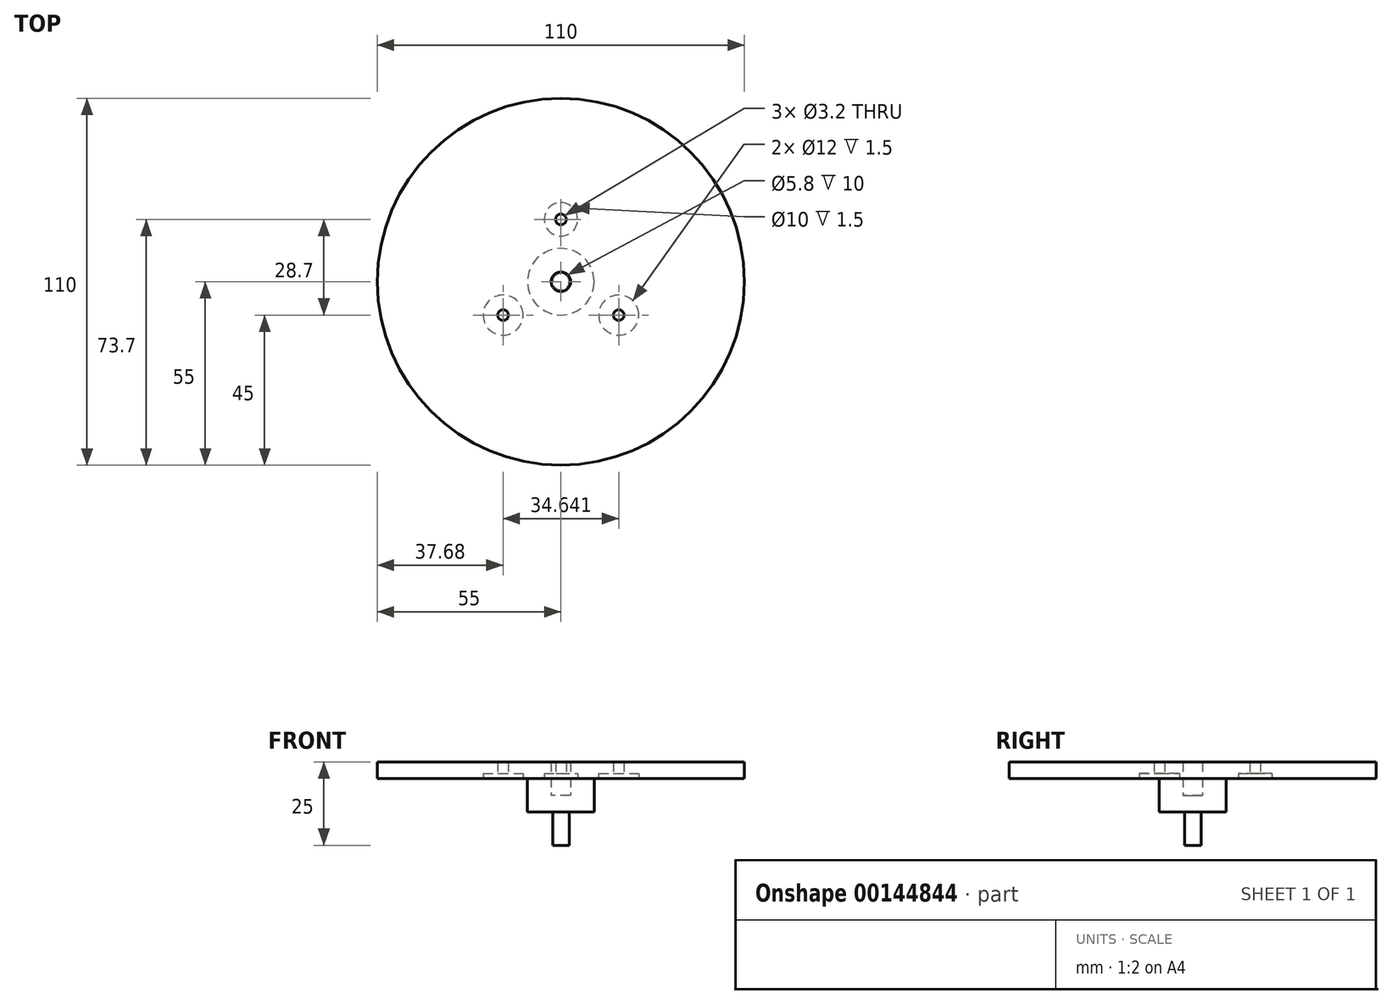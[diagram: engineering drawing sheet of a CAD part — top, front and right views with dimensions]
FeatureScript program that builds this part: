
annotation { "Feature Type Name" : "Feature", "Feature Type Description" : "" }
export const myFeature = defineFeature(function(context is Context, id is Id, definition is map)
    precondition{}
    {
        {
            var Q0;
            Q0=qCreatedBy(makeId("Top.planeOp"),FACE);
            var sketch = newSketch(context, id + "F0", { "sketchPlane" : qUnion([Q0])});
            skCircle(sketch, "E0", {"center": v(0, 0) * mm, "radius": 55 * mm});
            skCircle(sketch, "E1", {"center": v(0, 0) * mm, "radius": 2.9 * mm});
            skCircle(sketch, "E2", {"center": v(0, 18.7) * mm, "radius": 1.6 * mm});
            skLineSegment(sketch, "E3", {"start": v(0, 0) * mm, "end": v(0, 26.43) * mm, "construction": true});
            skLineSegment(sketch, "E4", {"start": v(0, 0) * mm, "end": v(-17.32, -10) * mm, "construction": true});
            skLineSegment(sketch, "E5", {"start": v(0, 0) * mm, "end": v(17.32, -10) * mm, "construction": true});
            skCircle(sketch, "E6", {"center": v(-17.32, -10) * mm, "radius": 1.6 * mm});
            skCircle(sketch, "E7", {"center": v(17.32, -10) * mm, "radius": 1.6 * mm});
            skSolve(sketch);
        }
        {
            var Q0;
            Q0 = qSketchRegion(id + "F0", true);
            extrude(context, id + "F1", {"entities" : qUnion([Q0]), "depth" : 5 * mm});
        }
        {
            var Q0;
            Q0=makeQuery(id+"F1.opExtrude","CAP_FACE",FACE,{"disambiguationData":[OSD([sQuery(id+"F0.wireOp",EDGE,"E0"),sQuery(id+"F0.wireOp",EDGE,"E1"),sQuery(id+"F0.wireOp",EDGE,"E2"),sQuery(id+"F0.wireOp",EDGE,"E6"),sQuery(id+"F0.wireOp",EDGE,"E7")])],"isStart":true});
            var sketch = newSketch(context, id + "F2", { "sketchPlane" : qUnion([Q0])});
            skCircle(sketch, "E8", {"center": v(0, 0) * mm, "radius": 10 * mm});
            skSolve(sketch);
        }
        {
            var Q0;
            Q0 = qSketchRegion(id + "F2", true);
            extrude(context, id + "F3", {"entities" : qUnion([Q0]), "operationType" : NewBodyOperationType.ADD, "depth" : 10 * mm});
        }
        {
            var Q0;
            Q0=makeQuery(id+"F1.opExtrude","CAP_FACE",FACE,{"disambiguationData":[OSD([sQuery(id+"F0.wireOp",EDGE,"E0"),sQuery(id+"F0.wireOp",EDGE,"E1"),sQuery(id+"F0.wireOp",EDGE,"E2"),sQuery(id+"F0.wireOp",EDGE,"E6"),sQuery(id+"F0.wireOp",EDGE,"E7")])],"isStart":false});
            var sketch = newSketch(context, id + "F4", { "sketchPlane" : qUnion([Q0])});
            skCircle(sketch, "E9", {"center": v(0, 0) * mm, "radius": 2.9 * mm});
            skSolve(sketch);
        }
        {
            var Q0;
            Q0 = qSketchRegion(id + "F4", true);
            extrude(context, id + "F5", {"entities" : qUnion([Q0]), "operationType" : NewBodyOperationType.REMOVE, "oppositeDirection" : true, "depth" : 10 * mm});
        }
        {
            var Q0;
            Q0=makeQuery(id+"F3.opExtrude","CAP_FACE",FACE,{"disambiguationData":[OSD([sQuery(id+"F2.wireOp",EDGE,"E8")])],"isStart":false});
            var sketch = newSketch(context, id + "F6", { "sketchPlane" : qUnion([Q0])});
            skCircle(sketch, "E10", {"center": v(0, 0) * mm, "radius": 2.5 * mm});
            skSolve(sketch);
        }
        {
            var Q0;
            Q0 = qSketchRegion(id + "F6", true);
            extrude(context, id + "F7", {"entities" : qUnion([Q0]), "operationType" : NewBodyOperationType.ADD, "depth" : 10 * mm});
        }
        {
            var Q0;
            Q0=makeQuery(id+"F1.opExtrude","CAP_FACE",FACE,{"disambiguationData":[OSD([sQuery(id+"F0.wireOp",EDGE,"E0"),sQuery(id+"F0.wireOp",EDGE,"E1"),sQuery(id+"F0.wireOp",EDGE,"E2"),sQuery(id+"F0.wireOp",EDGE,"E6"),sQuery(id+"F0.wireOp",EDGE,"E7")])],"isStart":true});
            var sketch = newSketch(context, id + "F8", { "sketchPlane" : qUnion([Q0])});
            skCircle(sketch, "E11", {"center": v(-17.32, 10) * mm, "radius": 6 * mm});
            skCircle(sketch, "E12", {"center": v(17.32, 10) * mm, "radius": 6 * mm});
            skCircle(sketch, "E13", {"center": v(0, -18.7) * mm, "radius": 5 * mm});
            skSolve(sketch);
        }
        {
            var Q0;
            Q0 = qSketchRegion(id + "F8", true);
            extrude(context, id + "F9", {"entities" : qUnion([Q0]), "operationType" : NewBodyOperationType.REMOVE, "oppositeDirection" : true, "depth" : 1.5 * mm});
        }
    });
